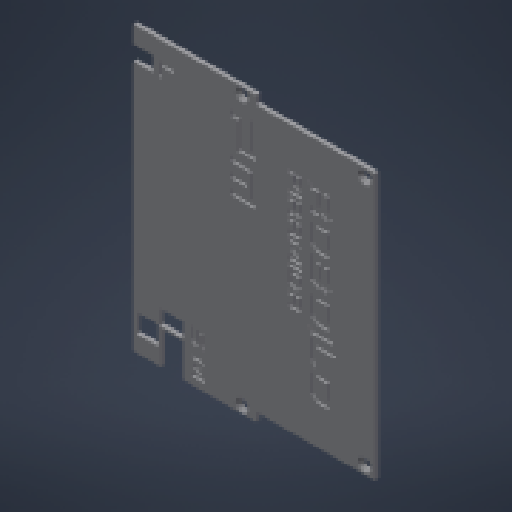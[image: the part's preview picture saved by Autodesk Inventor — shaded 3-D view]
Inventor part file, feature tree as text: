
AUTODESK INVENTOR PART (.ipt)
format: ipt  version: 2023 (Build 270158000, 158)  size: 442,368 bytes
history: native  units: mm
features: reference x14, other x11, sketch x3, extrude x2, hole x1, projected_geometry x1
ambient origin geometry x8: Origin, YZ Plane, XZ Plane, XY Plane, X Axis, Y Axis, Z Axis, Center Point
bodies: Body1 (feature_tree)
feature tree (32):
  other  "Bryła1"
  sketch  "Szkic1"
  other  "Płaszczyzna konstrukcyjna1"
  extrude  "Wyciągnięcie proste3"  Depth=2.0mm
  extrude  "Wyciągnięcie proste2"  Depth=1.0mm TaperAngle=0.0deg
  hole  "Hole1"  [1 undecoded]
  reference  "Odniesienie1"
  reference  "Odniesienie2"
  reference  "Odniesienie4"
  reference  "Odniesienie5"
  reference  "Odniesienie6"
  reference  "Odniesienie7"
  sketch  "Szkic2"
  reference  "Odniesienie8"
  projected_geometry  "Pętla rzutowana1"
  reference  "Odniesienie9"
  sketch  "Sketch3"  dims[d0=1.0mm d3=2.0mm d5=1.0mm d6=0.0mm d7=2.0mm d8=0.0mm d11=15.202mm d12=8.463mm d14=12.569mm d15=3.192mm d16=5.694mm d18=3.307mm d19=2.634mm d20=8.886mm d21=11.062mm d23=4.216mm d24=4.216mm d26=1.553mm d27=8.0mm d29=3.4mm d30=6.0mm d31=6.3mm d32=2.0mm d33=90.0deg d34=8.0mm d35=20.594885mm d36=1.0mm d37=1.5mm]
  reference  "Reference10"
  reference  "Reference11"
  reference  "Reference12"
  reference  "Reference13"
  reference  "Reference14"
  reference  "Reference15"
  parser-record x1  (decoder bookkeeping rows leaked as tree rows — omitted from the tree; the rows remain in map.json)
  other  "Zespół1.iam"
  other  "Bok2mm:1"
  other  "Bok2mm_MIR:1"
  other  "Tyl:1"
  other  "mocowanie_silnika_wariant1_MIR:1"
  other  "mocowanie_silnika_wariant1:1"
  other  "MocowanieCzujnikaBazSciankiLewy:1"
  other  "MocowanieCzujnikaBezScianki:1"
note: 1 required parameter value undecoded (feature->parameter linkage not recoverable at this tier; creation-order binding heuristic only, values carry confidence <= 0.55)
note: 1 file-system path scrubbed to <path> (originals preserved in map.json)
